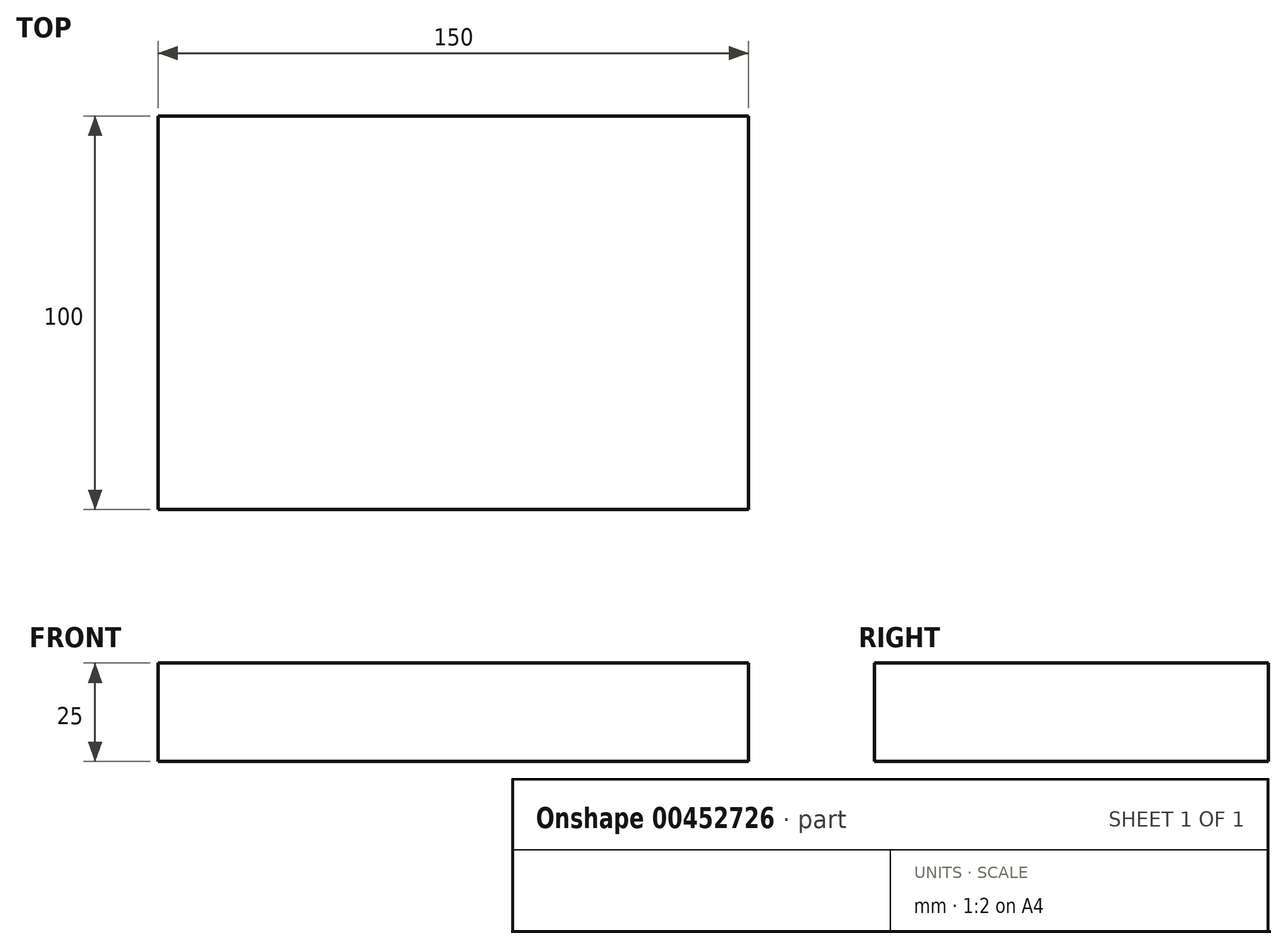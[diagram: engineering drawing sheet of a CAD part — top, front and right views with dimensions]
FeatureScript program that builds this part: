
annotation { "Feature Type Name" : "Feature", "Feature Type Description" : "" }
export const myFeature = defineFeature(function(context is Context, id is Id, definition is map)
    precondition{}
    {
        {
            var Q0;
            Q0=qCreatedBy(makeId("Top.planeOp"),FACE);
            var sketch = newSketch(context, id + "F0", { "sketchPlane" : qUnion([Q0])});
            skLineSegment(sketch, "E0.bottom", {"start": v(-75, 50) * mm, "end": v(75, 50) * mm});
            skLineSegment(sketch, "E0.top", {"start": v(-75, -50) * mm, "end": v(75, -50) * mm});
            skLineSegment(sketch, "E0.left", {"start": v(-75, 50) * mm, "end": v(-75, -50) * mm});
            skLineSegment(sketch, "E0.right", {"start": v(75, 50) * mm, "end": v(75, -50) * mm});
            skSolve(sketch);
        }
        {
            var Q0;
            Q0 = qSketchRegion(id + "F0", true);
            extrude(context, id + "F1", {"entities" : qUnion([Q0]), "oppositeDirection" : true, "depth" : 25 * mm});
        }
    });
